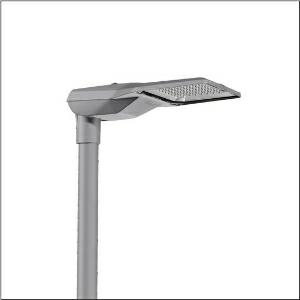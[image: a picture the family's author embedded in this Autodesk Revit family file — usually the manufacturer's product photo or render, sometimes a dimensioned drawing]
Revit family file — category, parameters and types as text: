
# Revit family: streetlight_sl_21_iq_midi___p0_5a_5xe3v31v08nb_978c
name_source: partatom
category: Lighting Fixtures
units: mm (PartAtom-declared; Revit-internal decimal feet)

## family parameters
Cut with Voids When Loaded = No
Host = Face
Light Source = No
Part Type = Normal
Room Calculation Point = No
Round Connector Dimension = Use Diameter
Shared = No

## types (1)
- --- (1 x LED, 21180 lm, 136.6 W, 3000K)
    Apparent Load = 137 VA
    CIE Flux Codes = 37 73 96 100 100
    Color Rendering = 70
    Color Temperature = 3000K
    Default Elevation = 1800 mm
    Description = Streetlight SL 21 iQ midi, mast luminaire, primary light control with lens, of PMMA, primary optical cover: cover, of toughened safety glass, transparent, light distribution: P0.5a, light emission: direct distribution, primary light characteristic: asymmetric, installation type: post-top, side-entry, LED, High Power LED, rated luminous flux: 21.180lm, luminous efficacy: 155lm/W, light colour: 730, colour temperature: 3000K, control gear: iQ-Street Remote, D4i with power reduction, control: pre-setting: logarithmic dimming characteristic, Street-Remote, Auto-Match, Temp-Guard, Lumen-Switch, Night-Set, Smart-Wire, Light-Fading, Desk-Remote (wireless, voltage-free reading and setting of iQ features in the workshop via application-optimized NFC function/RFID function), optimised constant luminous flux control (CLO 2.0), mains connection: 230..240V, AC, 50/60Hz, start of lifetime: 137W, end of service life: 144W, reduction: 61W, luminaire housing, of diecast aluminium, powder-coated, SITECO metallic grey (DB 702S), corrosivity category C5 high according to DIN EN ISO 12944, please order mast flange separately, inclination adjustable: 0°, 5°, 10°, 15°, sealing non-destructively replaceable, multi-level sealing system, length: 644mm, width: 335mm, height: 110mm, mast flange for spigot size: 42mm (side-entry): 5XC10008XM4, 60/48mm (side-entry/post-top): 5XC10108XM2, 76/60mm (side-entry/post-top): 5XC10108XM1, mounting height: 4..8m, Smart Interface above, protection rating (complete): IP66, insulation class (complete): insulation class II (safety insulation), certification: CE, ENEC, ENEC+, VDE, impact resistance: IK10, permissible operating ambient temperature for outdoor applications: -40..+50°C, standard-compliant lighting for roads and squares, packaging unit: 1 piece

Light Distribution: P0.5a
    Height = 111 mm
    Lamp = 1 x LED
    Lamp Light Flux = 21180 lm
    Lamp Power = 136.6 W
    Lamp count = 1
    Length = 644 mm
    Luminous efficacy = 155 lm/W
    Manufacturer = Siteco
    ModVariant = No
    Model = 5XE3V31V08NB
    Number of Poles = 1
    OnlyDefault = Yes
    Power Factor = 1
    Product Name = Streetlight SL 21 iQ midi | P0.5a
    Product group = mast luminaire | pylon top
    ProductGroupID = 6100
    Protection Class = Protection class II
    Protection Degree = IP 66
    RLX_Detail_Level = 1
    RLX_Emergency_Light_Flux = 0 lm
    RLX_Emergency_Type = 0
    RLX_Emergency_Type_DB = No
    RlxData = <blob elided: 90781 chars, md5=6cca1353>
    Socket = socket
    Standby Power = 0 W
    System Light Flux = 21180 lm
    System Power = 137 W
    Type Comments = factory setting: luminous flux: 100 % | dim-lin: 254 | 733 mA
    Type Image = l_1004302.jpg
    URL = http://relux.com
    VarID = @adj_077053
    Voltage = 0 V
    Weight = 0.00 kg
    Width = 336 mm

## geometry (parser evidence)
native form markers: Blend x4, Sweep x11
no freeform markers — native parametric forms only
